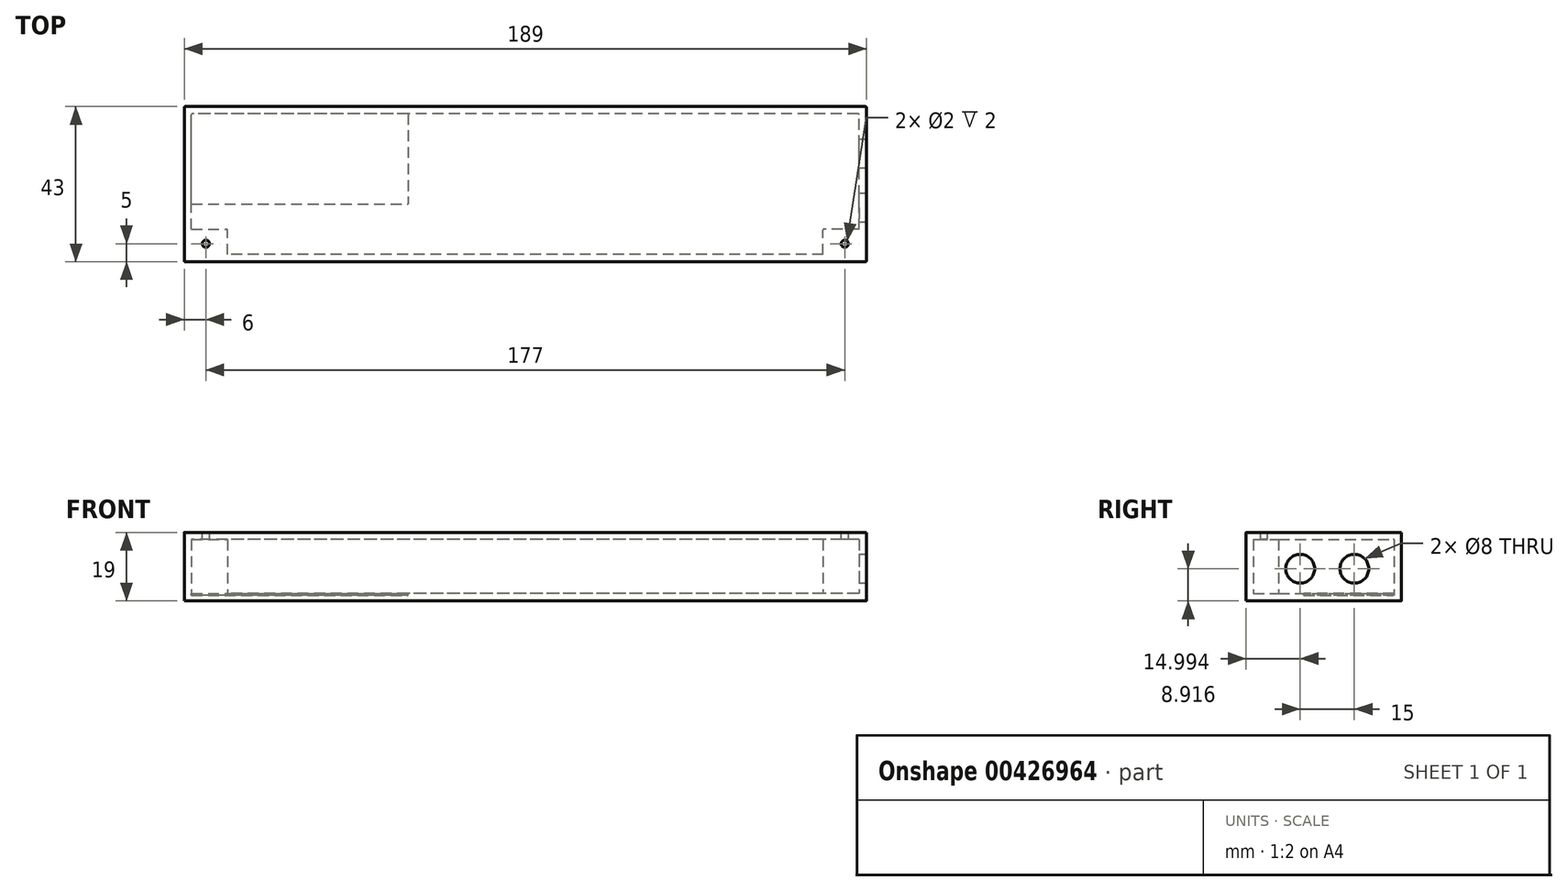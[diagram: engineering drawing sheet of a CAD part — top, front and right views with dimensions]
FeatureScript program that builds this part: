
annotation { "Feature Type Name" : "Feature", "Feature Type Description" : "" }
export const myFeature = defineFeature(function(context is Context, id is Id, definition is map)
    precondition{}
    {
        {
            var Q0;
            Q0=qCreatedBy(makeId("Top.planeOp"),FACE);
            var sketch = newSketch(context, id + "F0", { "sketchPlane" : qUnion([Q0])});
            skPoint(sketch, "E0.middle", {"position": v(0, 0) * mm});
            skLineSegment(sketch, "E1.bottom", {"start": v(94.5, -21.5) * mm, "end": v(-94.5, -21.5) * mm});
            skLineSegment(sketch, "E1.top", {"start": v(94.5, 21.5) * mm, "end": v(-94.5, 21.5) * mm});
            skLineSegment(sketch, "E1.left", {"start": v(94.5, -21.5) * mm, "end": v(94.5, 21.5) * mm});
            skLineSegment(sketch, "E1.right", {"start": v(-94.5, -21.5) * mm, "end": v(-94.5, 21.5) * mm});
            skSolve(sketch);
        }
        {
            var Q0;
            Q0 = qSketchRegion(id + "F0", true);
            extrude(context, id + "F1", {"entities" : qUnion([Q0]), "depth" : 17 * mm, "offsetDistance" : 25 * mm});
        }
        {
            var Q0;
            Q0=makeQuery(id+"F1.opExtrude","CAP_FACE",FACE,{"disambiguationData":[OSD([sQuery(id+"F0.wireOp",EDGE,"E1.bottom"),sQuery(id+"F0.wireOp",EDGE,"E1.top"),sQuery(id+"F0.wireOp",EDGE,"E1.left"),sQuery(id+"F0.wireOp",EDGE,"E1.right")])],"isStart":false});
            shell(context, id + "F2", {"entities" : qUnion([Q0]), "thickness" : 2 * mm});
        }
        {
            var Q0;
            Q0=makeQuery(id+"F1.opExtrude","SWEPT_FACE",FACE,{"disambiguationData":[OSD([sQuery(id+"F0.wireOp",EDGE,"E1.left")])]});
            var sketch = newSketch(context, id + "F3", { "sketchPlane" : qUnion([Q0])});
            skCircle(sketch, "E2", {"center": v(-6.5, 8.92) * mm, "radius": 4 * mm});
            skCircle(sketch, "E3", {"center": v(8.5, 8.92) * mm, "radius": 4 * mm});
            skSolve(sketch);
        }
        {
            var Q0;
            Q0 = qSketchRegion(id + "F3", true);
            extrude(context, id + "F4", {"entities" : qUnion([Q0]), "operationType" : NewBodyOperationType.REMOVE, "endBound" : BoundingType.UP_TO_NEXT, "oppositeDirection" : true, "depth" : 25 * mm, "offsetDistance" : 25 * mm});
        }
        {
            var Q0;
            Q0=makeQuery(id+"F2.opShell","OFFSET_FACE",FACE,{"disambiguationData":[OSD([sQuery(id+"F0.wireOp",EDGE,"E1.bottom"),sQuery(id+"F0.wireOp",EDGE,"E1.top"),sQuery(id+"F0.wireOp",EDGE,"E1.left"),sQuery(id+"F0.wireOp",EDGE,"E1.right")])]});
            var sketch = newSketch(context, id + "F5", { "sketchPlane" : qUnion([Q0])});
            skLineSegment(sketch, "E4.bottom", {"start": v(-92.5, -19.5) * mm, "end": v(-82.5, -19.5) * mm});
            skLineSegment(sketch, "E4.top", {"start": v(-92.5, -12.5) * mm, "end": v(-82.5, -12.5) * mm});
            skLineSegment(sketch, "E4.left", {"start": v(-92.5, -19.5) * mm, "end": v(-92.5, -12.5) * mm});
            skLineSegment(sketch, "E4.right", {"start": v(-82.5, -19.5) * mm, "end": v(-82.5, -12.5) * mm});
            skLineSegment(sketch, "E5.bottom", {"start": v(92.5, -19.5) * mm, "end": v(82.5, -19.5) * mm});
            skLineSegment(sketch, "E5.top", {"start": v(92.5, -12.5) * mm, "end": v(82.5, -12.5) * mm});
            skLineSegment(sketch, "E5.left", {"start": v(92.5, -19.5) * mm, "end": v(92.5, -12.5) * mm});
            skLineSegment(sketch, "E5.right", {"start": v(82.5, -19.5) * mm, "end": v(82.5, -12.5) * mm});
            skSolve(sketch);
        }
        {
            var Q0;
            Q0 = qSketchRegion(id + "F5", true);
            var Q1;
            Q1=makeQuery(id+"F1.opExtrude","CAP_FACE",FACE,{"disambiguationData":[OSD([sQuery(id+"F0.wireOp",EDGE,"E1.bottom"),sQuery(id+"F0.wireOp",EDGE,"E1.top"),sQuery(id+"F0.wireOp",EDGE,"E1.left"),sQuery(id+"F0.wireOp",EDGE,"E1.right")])],"isStart":false});
            extrude(context, id + "F6", {"entities" : qUnion([Q0]), "operationType" : NewBodyOperationType.ADD, "endBound" : BoundingType.UP_TO_SURFACE, "depth" : 25 * mm, "endBoundEntityFace" : qUnion([Q1]), "offsetDistance" : 25 * mm});
        }
        {
            var Q0;
            {var subQ0=sQuery(id+"F0.wireOp",EDGE,"E1.right");var subQ1=sQuery(id+"F0.wireOp",EDGE,"E1.left");var subQ2=sQuery(id+"F0.wireOp",EDGE,"E1.top");var subQ3=sQuery(id+"F0.wireOp",EDGE,"E1.bottom");Q0=makeQuery(id+"F6.boolean.opBoolean","MERGE",FACE,{"derivedFrom":[makeQuery(id+"F1.opExtrude","CAP_FACE",FACE,{"disambiguationData":[OSD([subQ3,subQ2,subQ1,subQ0])],"isStart":false}),makeQuery(id+"F6.opExtrude","CAP_FACE",FACE,{"disambiguationData":[OSD([subQ3,subQ2,subQ1,subQ0]),OD(0.0)],"isStart":false}),makeQuery(id+"F6.opExtrude","CAP_FACE",FACE,{"disambiguationData":[OSD([subQ3,subQ2,subQ1,subQ0]),OD(1.0)],"isStart":false})]});}
            var sketch = newSketch(context, id + "F7", { "sketchPlane" : qUnion([Q0])});
            skLineSegment(sketch, "E6.bottom", {"start": v(-94.5, 21.5) * mm, "end": v(94.5, 21.5) * mm});
            skLineSegment(sketch, "E6.top", {"start": v(-94.5, 19.5) * mm, "end": v(94.5, 19.5) * mm});
            skLineSegment(sketch, "E6.left", {"start": v(-94.5, 21.5) * mm, "end": v(-94.5, 19.5) * mm});
            skLineSegment(sketch, "E6.right", {"start": v(94.5, 21.5) * mm, "end": v(94.5, 19.5) * mm});
            skSolve(sketch);
        }
        {
            var Q0;
            Q0 = qSketchRegion(id + "F7", true);
            extrude(context, id + "F8", {"entities" : qUnion([Q0]), "operationType" : NewBodyOperationType.ADD, "depth" : 2 * mm, "offsetDistance" : 25 * mm});
        }
        {
            var Q0;
            Q0=makeQuery(id+"F8.boolean.opBoolean","MERGE",FACE,{"derivedFrom":[makeQuery(id+"F2.opShell","OFFSET_FACE",FACE,{"disambiguationData":[OSD([sQuery(id+"F0.wireOp",EDGE,"E1.top")])]}),makeQuery(id+"F8.opExtrude","SWEPT_FACE",FACE,{"disambiguationData":[OSD([sQuery(id+"F7.wireOp",EDGE,"E6.top")])]})]});
            var sketch = newSketch(context, id + "F9", { "sketchPlane" : qUnion([Q0])});
            skLineSegment(sketch, "E7.bottom", {"start": v(94.5, 17) * mm, "end": v(-94.5, 17) * mm});
            skLineSegment(sketch, "E7.top", {"start": v(94.5, 18) * mm, "end": v(-94.5, 18) * mm});
            skLineSegment(sketch, "E7.left", {"start": v(94.5, 17) * mm, "end": v(94.5, 18) * mm});
            skLineSegment(sketch, "E7.right", {"start": v(-94.5, 17) * mm, "end": v(-94.5, 18) * mm});
            skSolve(sketch);
        }
        {
            var Q0;
            Q0 = qSketchRegion(id + "F9", true);
            extrude(context, id + "F10", {"entities" : qUnion([Q0]), "operationType" : NewBodyOperationType.REMOVE, "oppositeDirection" : true, "depth" : 1 * mm, "offsetDistance" : 25 * mm});
        }
        {
            var Q0;
            Q0=makeQuery(id+"F2.opShell","OFFSET_FACE",FACE,{"disambiguationData":[OSD([sQuery(id+"F0.wireOp",EDGE,"E1.bottom"),sQuery(id+"F0.wireOp",EDGE,"E1.top"),sQuery(id+"F0.wireOp",EDGE,"E1.left"),sQuery(id+"F0.wireOp",EDGE,"E1.right")])]});
            var sketch = newSketch(context, id + "F11", { "sketchPlane" : qUnion([Q0])});
            skLineSegment(sketch, "E8.bottom", {"start": v(-92.5, 19.5) * mm, "end": v(-32.5, 19.5) * mm});
            skLineSegment(sketch, "E8.top", {"start": v(-92.5, -5.5) * mm, "end": v(-32.5, -5.5) * mm});
            skLineSegment(sketch, "E8.left", {"start": v(-92.5, 19.5) * mm, "end": v(-92.5, -5.5) * mm});
            skLineSegment(sketch, "E8.right", {"start": v(-32.5, 19.5) * mm, "end": v(-32.5, -5.5) * mm});
            skSolve(sketch);
        }
        {
            var Q0;
            Q0 = qSketchRegion(id + "F11", true);
            extrude(context, id + "F12", {"entities" : qUnion([Q0]), "operationType" : NewBodyOperationType.REMOVE, "oppositeDirection" : true, "depth" : .5 * mm, "offsetDistance" : 25 * mm});
        }
        {
            var Q0;
            {var subQ0=sQuery(id+"F0.wireOp",EDGE,"E1.right");var subQ1=sQuery(id+"F0.wireOp",EDGE,"E1.left");var subQ2=sQuery(id+"F0.wireOp",EDGE,"E1.top");var subQ3=sQuery(id+"F0.wireOp",EDGE,"E1.bottom");Q0=makeQuery(id+"F10.boolean.opBoolean","MERGE",FACE,{"derivedFrom":[makeQuery(id+"F6.boolean.opBoolean","MERGE",FACE,{"derivedFrom":[makeQuery(id+"F1.opExtrude","CAP_FACE",FACE,{"disambiguationData":[OSD([subQ3,subQ2,subQ1,subQ0])],"isStart":false}),makeQuery(id+"F6.opExtrude","CAP_FACE",FACE,{"disambiguationData":[OSD([subQ3,subQ2,subQ1,subQ0]),OD(0.0)],"isStart":false}),makeQuery(id+"F6.opExtrude","CAP_FACE",FACE,{"disambiguationData":[OSD([subQ3,subQ2,subQ1,subQ0]),OD(1.0)],"isStart":false})]}),makeQuery(id+"F10.opExtrude","SWEPT_FACE",FACE,{"disambiguationData":[OSD([sQuery(id+"F9.wireOp",EDGE,"rW4BjMuT-cFca-8O94-LCI3-7OPLKiewGU9V.bottom")])]})]});}
            var sketch = newSketch(context, id + "F13", { "sketchPlane" : qUnion([Q0])});
            skLineSegment(sketch, "E9.bottom", {"start": v(-94.5, -21.5) * mm, "end": v(94.5, -21.5) * mm});
            skLineSegment(sketch, "E9.top", {"start": v(-94.5, 19.5) * mm, "end": v(94.5, 19.5) * mm});
            skLineSegment(sketch, "E9.left", {"start": v(-94.5, -21.5) * mm, "end": v(-94.5, 19.5) * mm});
            skLineSegment(sketch, "E9.right", {"start": v(94.5, -21.5) * mm, "end": v(94.5, 19.5) * mm});
            skSolve(sketch);
        }
        {
            var Q0;
            Q0 = qSketchRegion(id + "F13", true);
            extrude(context, id + "F14", {"entities" : qUnion([Q0]), "depth" : 2 * mm, "offsetDistance" : 25 * mm});
        }
        {
            var Q0;
            Q0=makeQuery(id+"F2.opShell","OFFSET_EDGE",EDGE,{"disambiguationData":[OSD([sQuery(id+"F0.wireOp",EDGE,"E1.top"),sQuery(id+"F0.wireOp",EDGE,"E1.left")])]});
            var Q1;
            Q1=makeQuery(id+"F6.opExtrude","SWEPT_EDGE",EDGE,{"disambiguationData":[OSD([sQuery(id+"F5.wireOp",EDGE,"E5.top"),sQuery(id+"F5.wireOp",EDGE,"E5.right")])]});
            var Q2;
            Q2=makeQuery(id+"F6.opExtrude","SWEPT_EDGE",EDGE,{"disambiguationData":[OSD([sQuery(id+"F0.wireOp",EDGE,"E1.left"),sQuery(id+"F5.wireOp",EDGE,"E5.top"),sQuery(id+"F5.wireOp",EDGE,"E5.left")])]});
            var Q3;
            Q3=makeQuery(id+"F6.opExtrude","SWEPT_EDGE",EDGE,{"disambiguationData":[OSD([sQuery(id+"F0.wireOp",EDGE,"E1.bottom"),sQuery(id+"F5.wireOp",EDGE,"E5.bottom"),sQuery(id+"F5.wireOp",EDGE,"E5.right")])]});
            var Q4;
            Q4=makeQuery(id+"F12.boolean.opBoolean","MERGE",EDGE,{"derivedFrom":[makeQuery(id+"F2.opShell","OFFSET_EDGE",EDGE,{"disambiguationData":[OSD([sQuery(id+"F0.wireOp",EDGE,"E1.top"),sQuery(id+"F0.wireOp",EDGE,"E1.right")])]}),makeQuery(id+"F12.opExtrude","SWEPT_EDGE",EDGE,{"disambiguationData":[OSD([sQuery(id+"F11.wireOp",EDGE,"E8.bottom"),sQuery(id+"F11.wireOp",EDGE,"E8.left")])]})]});
            var Q5;
            Q5=makeQuery(id+"F6.opExtrude","SWEPT_EDGE",EDGE,{"disambiguationData":[OSD([sQuery(id+"F5.wireOp",EDGE,"E4.top"),sQuery(id+"F5.wireOp",EDGE,"E4.right")])]});
            var Q6;
            Q6=makeQuery(id+"F6.opExtrude","SWEPT_EDGE",EDGE,{"disambiguationData":[OSD([sQuery(id+"F0.wireOp",EDGE,"E1.bottom"),sQuery(id+"F5.wireOp",EDGE,"E4.bottom"),sQuery(id+"F5.wireOp",EDGE,"E4.right")])]});
            var Q7;
            Q7=makeQuery(id+"F6.opExtrude","SWEPT_EDGE",EDGE,{"disambiguationData":[OSD([sQuery(id+"F0.wireOp",EDGE,"E1.right"),sQuery(id+"F5.wireOp",EDGE,"E4.top"),sQuery(id+"F5.wireOp",EDGE,"E4.left")])]});
            var Q8;
            Q8=makeQuery(id+"F1.opExtrude","SWEPT_EDGE",EDGE,{"disambiguationData":[OSD([sQuery(id+"F0.wireOp",EDGE,"E1.bottom"),sQuery(id+"F0.wireOp",EDGE,"E1.right")])]});
            var Q9;
            Q9=makeQuery(id+"F8.boolean.opBoolean","MERGE",EDGE,{"derivedFrom":[makeQuery(id+"F1.opExtrude","SWEPT_EDGE",EDGE,{"disambiguationData":[OSD([sQuery(id+"F0.wireOp",EDGE,"E1.top"),sQuery(id+"F0.wireOp",EDGE,"E1.right")])]}),makeQuery(id+"F8.opExtrude","SWEPT_EDGE",EDGE,{"disambiguationData":[OSD([sQuery(id+"F7.wireOp",EDGE,"E6.bottom"),sQuery(id+"F7.wireOp",EDGE,"E6.left")])]})]});
            var Q10;
            Q10=makeQuery(id+"F1.opExtrude","SWEPT_EDGE",EDGE,{"disambiguationData":[OSD([sQuery(id+"F0.wireOp",EDGE,"E1.bottom"),sQuery(id+"F0.wireOp",EDGE,"E1.left")])]});
            var Q11;
            Q11=makeQuery(id+"F8.boolean.opBoolean","MERGE",EDGE,{"derivedFrom":[makeQuery(id+"F1.opExtrude","SWEPT_EDGE",EDGE,{"disambiguationData":[OSD([sQuery(id+"F0.wireOp",EDGE,"E1.top"),sQuery(id+"F0.wireOp",EDGE,"E1.left")])]}),makeQuery(id+"F8.opExtrude","SWEPT_EDGE",EDGE,{"disambiguationData":[OSD([sQuery(id+"F7.wireOp",EDGE,"E6.bottom"),sQuery(id+"F7.wireOp",EDGE,"E6.right")])]})]});
            fillet(context, id + "F15", {"entities" : qUnion([Q0, Q1, Q2, Q3, Q4, Q5, Q6, Q7, Q8, Q9, Q10, Q11]), "radius" : .25 * mm, "tangentPropagation" : true, "allowEdgeOverflow" : false});
        }
        {
            var Q0;
            Q0=makeQuery(id+"F14.opExtrude","SWEPT_EDGE",EDGE,{"disambiguationData":[OSD([sQuery(id+"F13.wireOp",EDGE,"E9.bottom"),sQuery(id+"F13.wireOp",EDGE,"E9.left")])]});
            var Q1;
            Q1=makeQuery(id+"F14.opExtrude","SWEPT_EDGE",EDGE,{"disambiguationData":[OSD([sQuery(id+"F13.wireOp",EDGE,"E9.bottom"),sQuery(id+"F13.wireOp",EDGE,"E9.right")])]});
            fillet(context, id + "F16", {"entities" : qUnion([Q0, Q1]), "radius" : .25 * mm, "tangentPropagation" : true, "allowEdgeOverflow" : false});
        }
        {
            var Q0;
            Q0=makeQuery(id+"F14.opExtrude","SWEPT_FACE",FACE,{"disambiguationData":[OSD([sQuery(id+"F13.wireOp",EDGE,"E9.top")])]});
            var sketch = newSketch(context, id + "F17", { "sketchPlane" : qUnion([Q0])});
            skLineSegment(sketch, "E10.bottom", {"start": v(94.5, 17) * mm, "end": v(-94.5, 17) * mm});
            skLineSegment(sketch, "E10.top", {"start": v(94.5, 18) * mm, "end": v(-94.5, 18) * mm});
            skLineSegment(sketch, "E10.left", {"start": v(94.5, 17) * mm, "end": v(94.5, 18) * mm});
            skLineSegment(sketch, "E10.right", {"start": v(-94.5, 17) * mm, "end": v(-94.5, 18) * mm});
            skSolve(sketch);
        }
        {
            var Q0;
            Q0 = qSketchRegion(id + "F17", true);
            extrude(context, id + "F18", {"entities" : qUnion([Q0]), "operationType" : NewBodyOperationType.ADD, "depth" : 1 * mm, "offsetDistance" : 25 * mm});
        }
        {
            var Q0;
            Q0=makeQuery(id+"F14.opExtrude","CAP_FACE",FACE,{"disambiguationData":[OSD([sQuery(id+"F13.wireOp",EDGE,"E9.bottom"),sQuery(id+"F13.wireOp",EDGE,"E9.top"),sQuery(id+"F13.wireOp",EDGE,"E9.left"),sQuery(id+"F13.wireOp",EDGE,"E9.right")])],"isStart":false});
            var sketch = newSketch(context, id + "F19", { "sketchPlane" : qUnion([Q0])});
            skCircle(sketch, "E11", {"center": v(-88.5, -16.5) * mm, "radius": 1 * mm});
            skCircle(sketch, "E12", {"center": v(88.5, -16.5) * mm, "radius": 1 * mm});
            skSolve(sketch);
        }
        {
            var Q0;
            Q0 = qSketchRegion(id + "F19", true);
            extrude(context, id + "F20", {"entities" : qUnion([Q0]), "operationType" : NewBodyOperationType.REMOVE, "oppositeDirection" : true, "depth" : 2 * mm, "offsetDistance" : 25 * mm});
        }
    });
